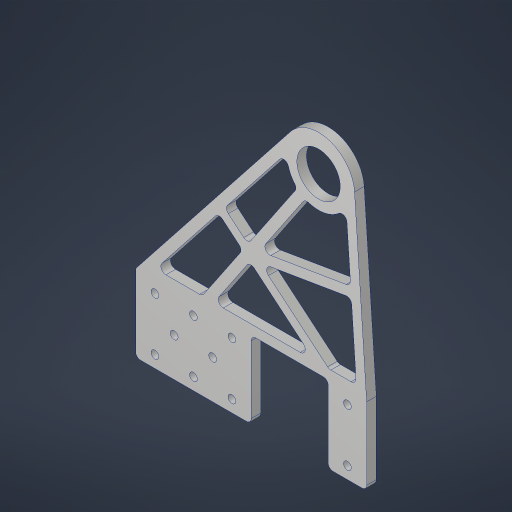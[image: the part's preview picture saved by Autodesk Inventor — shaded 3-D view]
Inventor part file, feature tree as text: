
AUTODESK INVENTOR PART (.ipt)
format: ipt  version: 2023.4 (Build 274418000, 418)  size: 349,184 bytes
history: native  units: in
note: dims shown in document units (in); Inventor stores cm internally (conversion verified against a paired STEP export)
features: sketch x3, extrude x2, fillet x2, hole x1, projected_geometry x1
ambient origin geometry x8: Origin, YZ Plane, XZ Plane, XY Plane, X Axis, Y Axis, Z Axis, Center Point
bodies: Solid1 (feature_tree)
feature tree (9):
  sketch  "Sketch1"  dims[d0=6.0in d1=2.0in]
  sketch  "Sketch2"  dims[d2=1.375in d3=0.5in d4=1.25in]
  extrude  "Extrusion1"  Depth=2.0in
  hole  "Hole1"  [1 undecoded]
  fillet  "Fillet1"  Radius=1.25in
  extrude  "Extrusion2"  Depth=0.13in
  fillet  "Fillet2"  Radius=1.0in
  sketch  "Sketch3"  dims[d5=1.25in d6=1.375in d7=1.0in d8=0.375in d9=0.5in d10=0.5in d11=0.5in d12=0.5in d13=0.5in d14=4.38in d15=5.0in d16=3.0in d17=1.125in d18=0.375in d20=0.375in d21=0.375in d22=0.25in d23=0.0in d24=0.201in d25=0.75in d26=0.375in d27=0.25in d28=0.5635in d29=1.0in d30=0.8108in d31=6.5in d32=0.75in d33=0.125in d34=0.25in d35=0.25in d36=0.125in d37=0.125in d38=0.125in d39=0.125in d40=0.125in d41=0.125in d42=0.0in d43=0.0in d44=0.13in]
  projected_geometry  "Project Cut Edges1"
note: 1 required parameter value undecoded (feature->parameter linkage not recoverable at this tier; creation-order binding heuristic only, values carry confidence <= 0.55)
